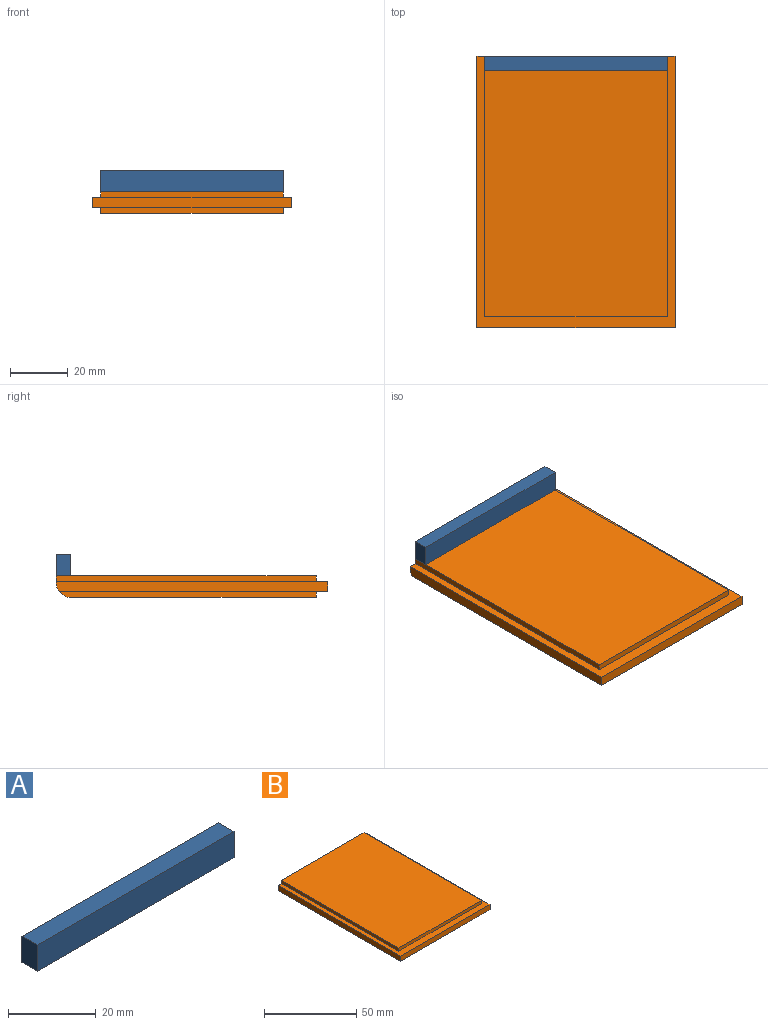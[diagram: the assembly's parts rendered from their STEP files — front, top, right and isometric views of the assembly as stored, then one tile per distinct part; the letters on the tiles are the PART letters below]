
ASSEMBLY  parts=2 mates=1
PART A: 6 faces, bbox 63.5x5x7.3 mm
  f0: plane 63.5x5mm, normal (0,0,1), area 317.5mm2, adj f1,f3,f4,f5
  f1: plane 7.3x5mm, normal (-1,0,0), area 36.5mm2, adj f0,f2,f4,f5
  f2: plane 63.5x5mm, normal (0,0,-1), area 317.5mm2, adj f1,f3,f4,f5
  f3: plane 7.3x5mm, normal (1,0,0), area 36.5mm2, adj f0,f2,f4,f5
  f4: plane 63.5x7.3mm, normal (0,-1,0), area 463.5mm2, adj f0,f1,f2,f3
  f5: plane 63.5x7.3mm, normal (0,1,0), area 463.5mm2, adj f0,f1,f2,f3
PART B: 15 faces, bbox 68.4x93.8x7.5 mm
  f0: plane 93.8x68.4mm, normal (0,0,1), area 740.5mm2, adj f2,f3,f4,f5,f11,f12,f13
  f1: plane 92.83x68.4mm, normal (0,0,-1), area 735.5mm2, adj f2,f3,f4,f6,f8,f9,f14
  f2: plane 93.8x3.4mm, normal (-1,0,0), area 318mm2, adj f0,f1,f4,f5,f14
  f3: plane 93.8x3.4mm, normal (1,0,0), area 318mm2, adj f0,f1,f4,f5,f14
  f4: plane 68.4x3.4mm, normal (0,-1,0), area 232.6mm2, adj f0,f1,f2,f3
  f5: plane 68.4x2.5mm, normal (0,1,0), area 160.3mm2, adj f0,f2,f3,f10,f11,f12,f14
  f6: plane 88.83x2.05mm, normal (-1,0,0), area 179.6mm2, adj f1,f7,f9,f14
  f7: plane 84.8x63.2mm, normal (0,0,-1), area 5359.2mm2, adj f6,f8,f9,f14
  f8: plane 88.83x2.05mm, normal (1,0,0), area 179.6mm2, adj f1,f7,f9,f14
  f9: plane 63.2x2.05mm, normal (0,-1,0), area 129.6mm2, adj f1,f6,f7,f8
  f10: plane 89.8x63.2mm, normal (0,0,1), area 5675.2mm2, adj f5,f11,f12,f13
  f11: plane 89.8x2.05mm, normal (-1,0,0), area 184.1mm2, adj f0,f5,f10,f13
  f12: plane 89.8x2.05mm, normal (1,0,0), area 184.1mm2, adj f0,f5,f10,f13
  f13: plane 63.2x2.05mm, normal (0,-1,0), area 129.6mm2, adj f0,f10,f11,f12
  f14: cylinder r=5mm len=68.4mm, axis (1,0,0), area 512.8mm2, adj f1,f2,f3,f5,f6,f7,f8
PLACE A at identity
PLACE B t=(-1.24,0,5.54)mm
MATE fastened B.f10 <-> A.f2  axis (0,0,1) through (0.36,0,9.01)mm
